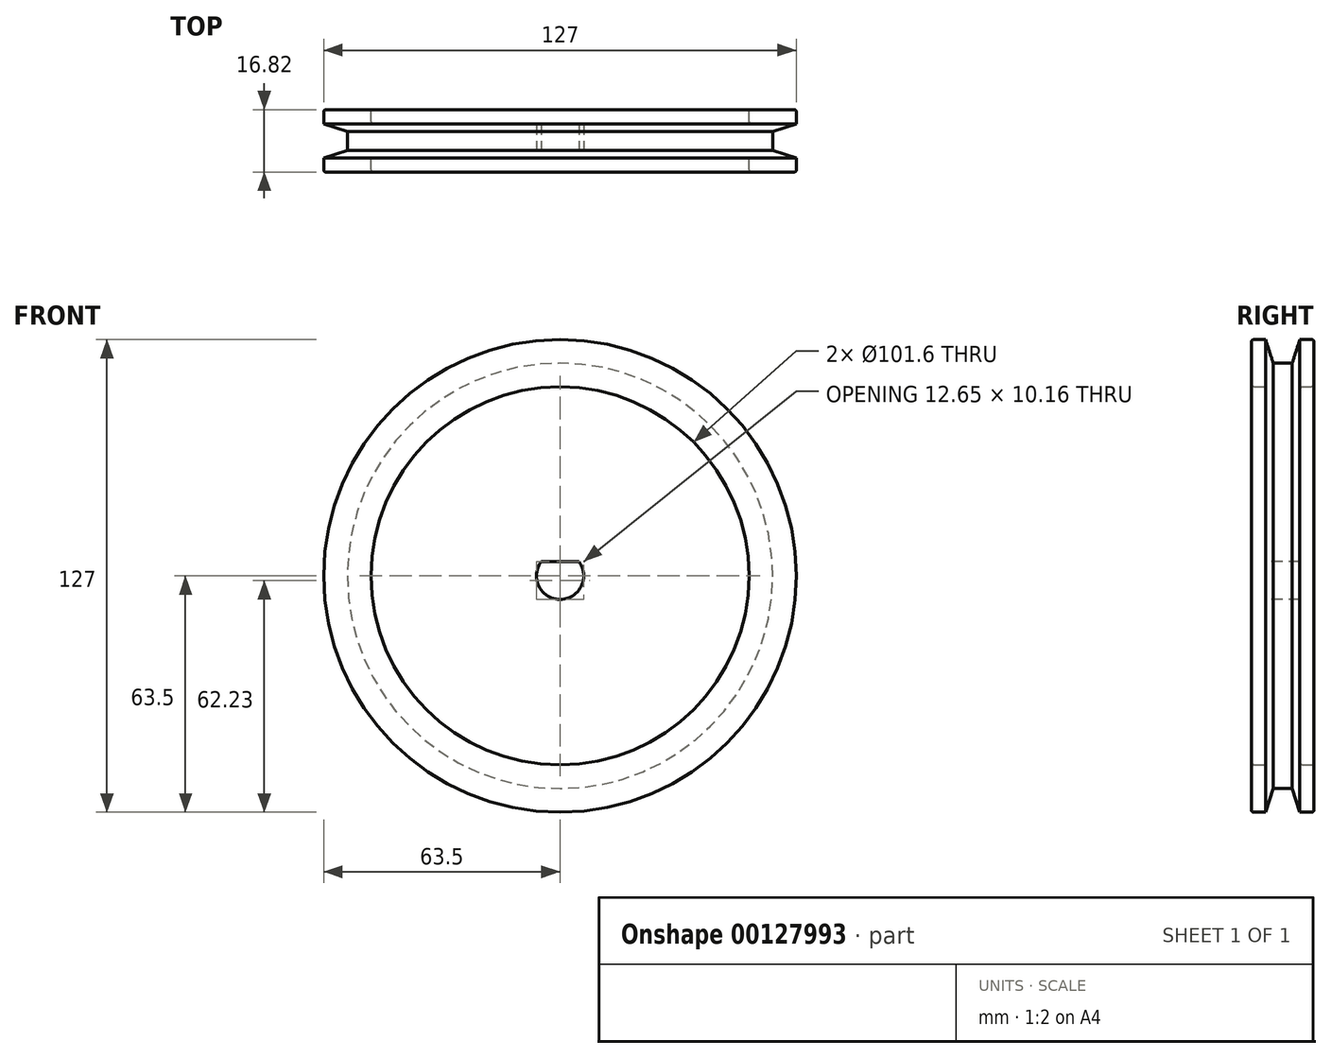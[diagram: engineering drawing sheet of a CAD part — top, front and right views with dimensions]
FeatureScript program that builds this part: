
annotation { "Feature Type Name" : "Feature", "Feature Type Description" : "" }
export const myFeature = defineFeature(function(context is Context, id is Id, definition is map)
    precondition{}
    {
        {
            var Q0;
            Q0=qCreatedBy(makeId("Right.planeOp"),FACE);
            var sketch = newSketch(context, id + "F0", { "sketchPlane" : qUnion([Q0])});
            skLineSegment(sketch, "E0", {"start": v(0, 57.15) * mm, "end": v(-2.54, 57.15) * mm});
            skLineSegment(sketch, "E1", {"start": v(-2.54, 57.15) * mm, "end": v(-4.6, 63.5) * mm});
            skLineSegment(sketch, "E2", {"start": v(-4.6, 63.5) * mm, "end": v(-7.78, 63.5) * mm});
            skLineSegment(sketch, "E3", {"start": v(-8.41, 62.87) * mm, "end": v(-8.41, 51.43) * mm});
            skLineSegment(sketch, "E4", {"start": v(-7.78, 50.8) * mm, "end": v(-5.24, 50.8) * mm});
            skLineSegment(sketch, "E5", {"start": v(-4.6, 50.16) * mm, "end": v(-4.6, 6.35) * mm});
            skPoint(sketch, "E6.visualSharp", {"position": v(-8.41, 63.5) * mm});
            skArc(sketch, "E6.filletArc", {"start": v(-7.78, 63.5) * mm, "mid": v(-8.23, 63.31) * mm, "end": v(-8.41, 62.87) * mm});
            skPoint(sketch, "E7.visualSharp", {"position": v(-8.41, 50.8) * mm});
            skArc(sketch, "E7.filletArc", {"start": v(-8.41, 51.43) * mm, "mid": v(-8.23, 50.99) * mm, "end": v(-7.78, 50.8) * mm});
            skPoint(sketch, "E8.visualSharp", {"position": v(-4.6, 50.8) * mm});
            skArc(sketch, "E8.filletArc", {"start": v(-4.6, 50.16) * mm, "mid": v(-4.79, 50.61) * mm, "end": v(-5.24, 50.8) * mm});
            skLineSegment(sketch, "E9.MirrorCS", {"start": v(7.78, 50.8) * mm, "end": v(5.24, 50.8) * mm});
            skArc(sketch, "E10.MirrorCS", {"start": v(4.6, 50.16) * mm, "mid": v(4.79, 50.61) * mm, "end": v(5.24, 50.8) * mm});
            skArc(sketch, "E11.MirrorCS", {"start": v(8.41, 51.43) * mm, "mid": v(8.23, 50.99) * mm, "end": v(7.78, 50.8) * mm});
            skLineSegment(sketch, "E12.MirrorCS", {"start": v(4.6, 63.5) * mm, "end": v(7.78, 63.5) * mm});
            skArc(sketch, "E13.MirrorCS", {"start": v(7.78, 63.5) * mm, "mid": v(8.23, 63.31) * mm, "end": v(8.41, 62.87) * mm});
            skLineSegment(sketch, "E14.MirrorCS", {"start": v(2.54, 57.15) * mm, "end": v(4.6, 63.5) * mm});
            skLineSegment(sketch, "E15.MirrorCS", {"start": v(0, 57.15) * mm, "end": v(2.54, 57.15) * mm});
            skPoint(sketch, "E16.MirrorP", {"position": v(4.6, 50.8) * mm});
            skPoint(sketch, "E17.MirrorP", {"position": v(8.41, 50.8) * mm});
            skLineSegment(sketch, "E18.MirrorCS", {"start": v(4.6, 50.16) * mm, "end": v(4.6, 6.35) * mm});
            skLineSegment(sketch, "E19.MirrorCS", {"start": v(8.41, 62.87) * mm, "end": v(8.41, 51.43) * mm});
            skPoint(sketch, "E20.MirrorP", {"position": v(8.41, 63.5) * mm});
            skPoint(sketch, "E21.orphan", {"position": v(-4.6, 0) * mm});
            skPoint(sketch, "E22.orphan", {"position": v(4.6, 0) * mm});
            skLineSegment(sketch, "E23.top", {"start": v(4.6, 0) * mm, "end": v(-4.6, 0) * mm});
            skLineSegment(sketch, "E23.left", {"start": v(4.6, 6.35) * mm, "end": v(4.6, 0) * mm});
            skLineSegment(sketch, "E23.right", {"start": v(-4.6, 6.35) * mm, "end": v(-4.6, 0) * mm});
            skSolve(sketch);
        }
        {
            var Q0;
            Q0=qCreatedBy(makeId("Top.planeOp"),FACE);
            var sketch = newSketch(context, id + "F1", { "sketchPlane" : qUnion([Q0])});
            skLineSegment(sketch, "E24", {"start": v(0, 0) * mm, "end": v(0, -28.22) * mm, "construction": true});
            skSolve(sketch);
        }
        {
            var Q0;
            Q0 = qSketchRegion(id + "F0", true);
            var Q1;
            Q1=sQuery(id+"F1.wireOp",EDGE,"E24");
            revolve(context, id + "F2", {"entities" : qUnion([Q0]), "axis" : qUnion([Q1]), "revolveType" : RevolveType.FULL});
        }
        {
            var Q0;
            Q0=makeQuery(id+"F2.opRevolve","SWEPT_FACE",FACE,{"disambiguationData":[OSD([sQuery(id+"F0.wireOp",EDGE,"E3")])]});
            cPlane(context, id + "F3", {"entities" : qUnion([Q0]), "cplaneType" : CPlaneType.OFFSET, "offset" : 25.4 * mm, "width" : 152.4 * mm, "height" : 152.4 * mm});
        }
        {
            var Q0;
            Q0=qCreatedBy(id+"F3.planeOp",FACE);
            var sketch = newSketch(context, id + "F4", { "sketchPlane" : qUnion([Q0])});
            skArc(sketch, "E25", {"start": v(-5.08, 3.81) * mm, "mid": v(0, -6.35) * mm, "end": v(5.08, 3.8) * mm});
            skLineSegment(sketch, "E26", {"start": v(5.08, 3.81) * mm, "end": v(-5.08, 3.81) * mm});
            skSolve(sketch);
        }
        {
            var Q0;
            Q0 = qSketchRegion(id + "F4", true);
            extrude(context, id + "F5", {"entities" : qUnion([Q0]), "operationType" : NewBodyOperationType.REMOVE, "endBound" : BoundingType.THROUGH_ALL, "oppositeDirection" : true, "depth" : 25.4 * mm});
        }
    });
